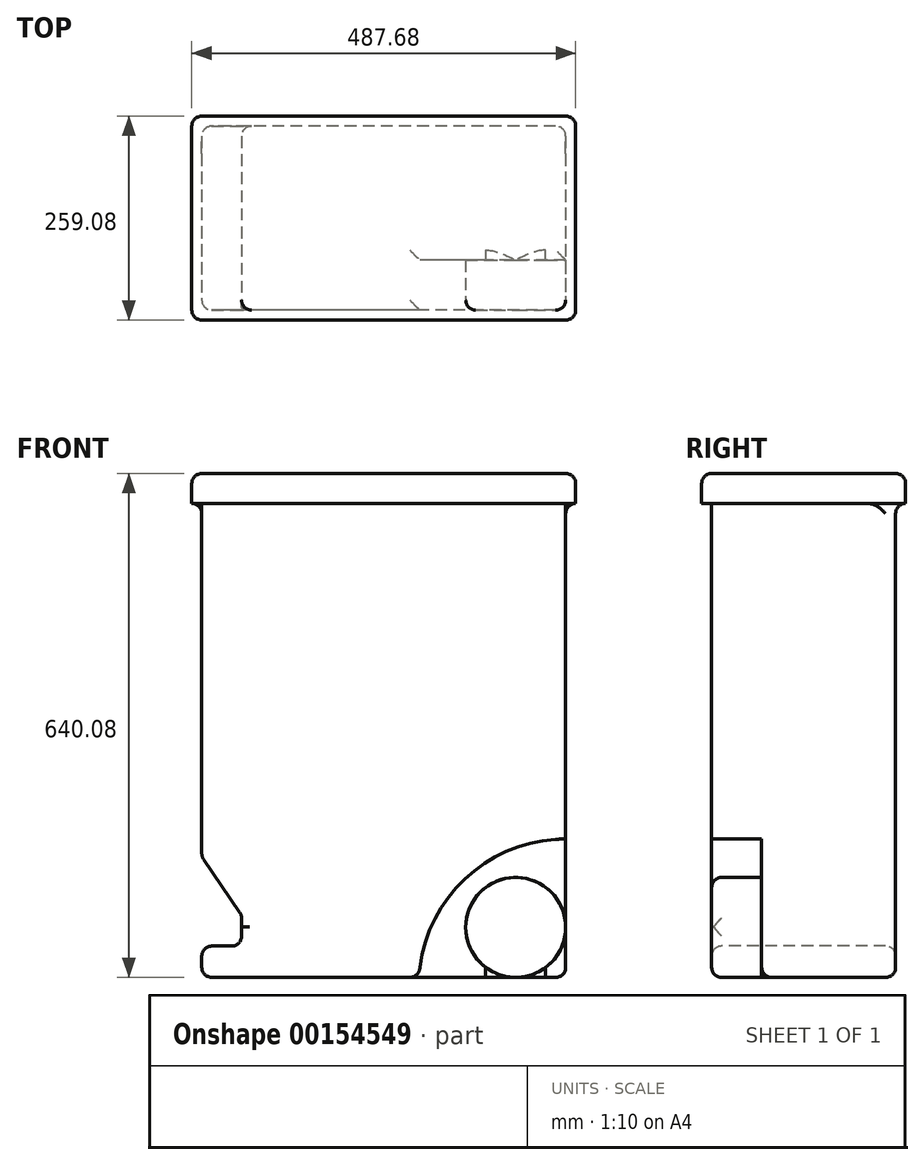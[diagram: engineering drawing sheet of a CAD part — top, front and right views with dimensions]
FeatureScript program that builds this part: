
annotation { "Feature Type Name" : "Feature", "Feature Type Description" : "" }
export const myFeature = defineFeature(function(context is Context, id is Id, definition is map)
    precondition{}
    {
        {
            var Q0;
            Q0=qCreatedBy(makeId("Top.planeOp"),FACE);
            var sketch = newSketch(context, id + "F0", { "sketchPlane" : qUnion([Q0])});
            skLineSegment(sketch, "E0.bottom", {"start": v(231.14, 116.84) * mm, "end": v(-231.14, 116.84) * mm});
            skLineSegment(sketch, "E0.top", {"start": v(231.14, -116.84) * mm, "end": v(-231.14, -116.84) * mm});
            skLineSegment(sketch, "E0.left", {"start": v(231.14, 116.84) * mm, "end": v(231.14, -116.84) * mm});
            skLineSegment(sketch, "E0.right", {"start": v(-231.14, 116.84) * mm, "end": v(-231.14, -116.84) * mm});
            skPoint(sketch, "E0.middle", {"position": v(0, 0) * mm});
            skSolve(sketch);
        }
        {
            var Q0;
            Q0=makeQuery(id+"F0.imprint","IMPRINT",FACE,{"disambiguationData":[TD([[makeQuery(id+"F0.imprint","IMPRINT",EDGE,{"derivedFrom":sQuery(id+"F0.wireOp",EDGE,"E0.bottom")}),1.0]])]});
            extrude(context, id + "F1", {"entities" : qUnion([Q0]), "depth" : 640.08 * mm});
        }
        {
            var Q0;
            Q0=makeQuery(id+"F1.opExtrude","CAP_FACE",FACE,{"disambiguationData":[OSD([sQuery(id+"F0.wireOp",EDGE,"E0.bottom"),sQuery(id+"F0.wireOp",EDGE,"E0.top"),sQuery(id+"F0.wireOp",EDGE,"E0.left"),sQuery(id+"F0.wireOp",EDGE,"E0.right")])],"isStart":false});
            var sketch = newSketch(context, id + "F2", { "sketchPlane" : qUnion([Q0])});
            skLineSegment(sketch, "E1.0", {"start": v(243.84, -129.54) * mm, "end": v(-243.84, -129.54) * mm});
            skLineSegment(sketch, "E1.1", {"start": v(243.84, 129.54) * mm, "end": v(243.84, -129.54) * mm});
            skLineSegment(sketch, "E1.2", {"start": v(243.84, 129.54) * mm, "end": v(-243.84, 129.54) * mm});
            skLineSegment(sketch, "E1.3", {"start": v(-243.84, 129.54) * mm, "end": v(-243.84, -129.54) * mm});
            skSolve(sketch);
        }
        {
            var Q0;
            Q0=makeQuery(id+"F2.imprint","IMPRINT",FACE,{"disambiguationData":[TD([[makeQuery(id+"F2.imprint","IMPRINT",EDGE,{"derivedFrom":sQuery(id+"F2.wireOp",EDGE,"E1.0")}),-1.0]])]});
            extrude(context, id + "F3", {"entities" : qUnion([Q0]), "operationType" : NewBodyOperationType.ADD, "oppositeDirection" : true, "depth" : 38.1 * mm});
        }
        {
            var Q0;
            Q0=qCreatedBy(makeId("Front.planeOp"),FACE);
            var sketch = newSketch(context, id + "F4", { "sketchPlane" : qUnion([Q0])});
            skLineSegment(sketch, "E2", {"start": v(-231.14, 153.28) * mm, "end": v(-180.63, 79.53) * mm});
            skLineSegment(sketch, "E3", {"start": v(-180.63, 79.53) * mm, "end": v(-180.63, 0) * mm});
            skLineSegment(sketch, "E4.0", {"start": v(231.14, 0) * mm, "end": v(-231.14, 0) * mm});
            skLineSegment(sketch, "E4.1", {"start": v(-231.14, 601.98) * mm, "end": v(-231.14, 0) * mm});
            skLineSegment(sketch, "E5", {"start": v(-180.63, 39.77) * mm, "end": v(-231.14, 39.77) * mm});
            skSolve(sketch);
        }
        {
            var Q0;
            {var subQ0=sQuery(id+"F4.wireOp",EDGE,"E2");Q0=makeQuery(id+"F4.imprint","IMPRINT",FACE,{"disambiguationData":[TD([[makeQuery(id+"F4.imprint","IMPRINT",EDGE,{"derivedFrom":subQ0}),-1.0]])]});}
            extrude(context, id + "F5", {"entities" : qUnion([Q0]), "operationType" : NewBodyOperationType.REMOVE, "oppositeDirection" : true, "depth" : 304.8 * mm, "symmetric" : true});
        }
        {
            var Q0;
            Q0=makeQuery(id+"F1.opExtrude","SWEPT_FACE",FACE,{"disambiguationData":[OSD([sQuery(id+"F0.wireOp",EDGE,"E0.top")])]});
            var sketch = newSketch(context, id + "F6", { "sketchPlane" : qUnion([Q0])});
            skCircle(sketch, "E6", {"center": v(167.64, 63.5) * mm, "radius": 63.5 * mm});
            skCircle(sketch, "E7", {"center": v(231.14, -10.9) * mm, "radius": 186.7 * mm});
            skLineSegment(sketch, "E8.0", {"start": v(231.14, 601.98) * mm, "end": v(231.14, 0) * mm});
            skLineSegment(sketch, "E8.1", {"start": v(231.14, 0) * mm, "end": v(-231.14, 0) * mm});
            skSolve(sketch);
        }
        {
            var Q0;
            {var subQ0=sQuery(id+"F6.wireOp",EDGE,"E8.0");var subQ1=sQuery(id+"F6.wireOp",EDGE,"E6");var subQ2=makeQuery(id+"F6.imprint","INTERSECT",VERTEX,{"derivedFrom":[subQ1,subQ0]});Q0=makeQuery(id+"F6.imprint","IMPRINT",FACE,{"disambiguationData":[TD([[makeQuery(id+"F6.imprint","IMPRINT",EDGE,{"disambiguationData":[TD([[subQ2,-1.0]])],"derivedFrom":subQ1}),-1.0]])]});}
            var Q1;
            {var subQ0=sQuery(id+"F6.wireOp",EDGE,"E8.0");var subQ1=sQuery(id+"F6.wireOp",EDGE,"E6");var subQ2=makeQuery(id+"F6.imprint","INTERSECT",VERTEX,{"derivedFrom":[subQ1,subQ0]});Q1=makeQuery(id+"F6.imprint","IMPRINT",FACE,{"disambiguationData":[TD([[makeQuery(id+"F6.imprint","IMPRINT",EDGE,{"disambiguationData":[TD([[subQ2,1.0]])],"derivedFrom":subQ1}),-1.0]])]});}
            extrude(context, id + "F7", {"entities" : qUnion([Q0, Q1]), "operationType" : NewBodyOperationType.REMOVE, "oppositeDirection" : true, "depth" : 63.5 * mm});
        }
        {
            var Q0;
            Q0=makeQuery(id+"F1.opExtrude","SWEPT_EDGE",EDGE,{"disambiguationData":[OSD([sQuery(id+"F0.wireOp",EDGE,"E0.top"),sQuery(id+"F0.wireOp",EDGE,"E0.right")])]});
            var Q1;
            Q1=makeQuery(id+"F1.opExtrude","SWEPT_EDGE",EDGE,{"disambiguationData":[OSD([sQuery(id+"F0.wireOp",EDGE,"E0.bottom"),sQuery(id+"F0.wireOp",EDGE,"E0.right")])]});
            var Q2;
            Q2=makeQuery(id+"F1.opExtrude","SWEPT_EDGE",EDGE,{"disambiguationData":[OSD([sQuery(id+"F0.wireOp",EDGE,"E0.bottom"),sQuery(id+"F0.wireOp",EDGE,"E0.left")])]});
            var Q3;
            Q3=makeQuery(id+"F1.opExtrude","SWEPT_EDGE",EDGE,{"disambiguationData":[OSD([sQuery(id+"F0.wireOp",EDGE,"E0.top"),sQuery(id+"F0.wireOp",EDGE,"E0.left")])]});
            var Q4;
            {var subQ0=sQuery(id+"F0.wireOp",EDGE,"E0.right");var subQ1=sQuery(id+"F0.wireOp",EDGE,"E0.left");var subQ2=sQuery(id+"F0.wireOp",EDGE,"E0.top");var subQ3=sQuery(id+"F0.wireOp",EDGE,"E0.bottom");Q4=makeQuery(id+"F3.boolean.opBoolean","MERGE",FACE,{"derivedFrom":[makeQuery(id+"F1.opExtrude","CAP_FACE",FACE,{"disambiguationData":[OSD([subQ3,subQ2,subQ1,subQ0])],"isStart":false}),makeQuery(id+"F3.opExtrude","CAP_FACE",FACE,{"disambiguationData":[OSD([subQ3,subQ2,subQ1,subQ0,sQuery(id+"F2.wireOp",EDGE,"E1.0"),sQuery(id+"F2.wireOp",EDGE,"E1.1"),sQuery(id+"F2.wireOp",EDGE,"E1.2"),sQuery(id+"F2.wireOp",EDGE,"E1.3")])],"isStart":true})]});}
            var Q5;
            Q5=makeQuery(id+"F3.opExtrude","SWEPT_EDGE",EDGE,{"disambiguationData":[OSD([sQuery(id+"F2.wireOp",EDGE,"E1.1"),sQuery(id+"F2.wireOp",EDGE,"E1.2")])]});
            var Q6;
            Q6=makeQuery(id+"F3.opExtrude","SWEPT_EDGE",EDGE,{"disambiguationData":[OSD([sQuery(id+"F2.wireOp",EDGE,"E1.2"),sQuery(id+"F2.wireOp",EDGE,"E1.3")])]});
            var Q7;
            Q7=makeQuery(id+"F3.opExtrude","SWEPT_EDGE",EDGE,{"disambiguationData":[OSD([sQuery(id+"F2.wireOp",EDGE,"E1.0"),sQuery(id+"F2.wireOp",EDGE,"E1.1")])]});
            var Q8;
            Q8=makeQuery(id+"F3.opExtrude","SWEPT_EDGE",EDGE,{"disambiguationData":[OSD([sQuery(id+"F2.wireOp",EDGE,"E1.0"),sQuery(id+"F2.wireOp",EDGE,"E1.3")])]});
            var Q9;
            Q9=makeQuery(id+"F5.boolean.opBoolean","COPY",EDGE,{"derivedFrom":makeQuery(id+"F5.opExtrude","SWEPT_EDGE",EDGE,{"disambiguationData":[OSD([sQuery(id+"F4.wireOp",EDGE,"E2"),sQuery(id+"F4.wireOp",EDGE,"E4.1")])]})});
            var Q10;
            Q10=makeQuery(id+"F5.boolean.opBoolean","COPY",FACE,{"derivedFrom":makeQuery(id+"F5.opExtrude","SWEPT_FACE",FACE,{"disambiguationData":[OSD([sQuery(id+"F4.wireOp",EDGE,"E2")])]})});
            var Q11;
            Q11=makeQuery(id+"F5.boolean.opBoolean","COPY",EDGE,{"derivedFrom":makeQuery(id+"F5.opExtrude","SWEPT_EDGE",EDGE,{"disambiguationData":[OSD([sQuery(id+"F4.wireOp",EDGE,"E4.1"),sQuery(id+"F4.wireOp",EDGE,"E5")])]})});
            var Q12;
            Q12=makeQuery(id+"F5.boolean.opBoolean","COPY",FACE,{"derivedFrom":makeQuery(id+"F5.opExtrude","SWEPT_FACE",FACE,{"disambiguationData":[OSD([sQuery(id+"F4.wireOp",EDGE,"E5")])]})});
            var Q13;
            Q13=makeQuery(id+"FMVX19U1BdIDMrO_1.1.F7.boolean.opBoolean","COPY",EDGE,{"derivedFrom":makeQuery(id+"FMVX19U1BdIDMrO_1.1.F7.opExtrude","CAP_EDGE",EDGE,{"disambiguationData":[OSD([sQuery(id+"F6.wireOp",EDGE,"E7")])],"isStart":true})});
            var Q14;
            {var subQ0=sQuery(id+"F6.wireOp",EDGE,"E6");var subQ1=makeQuery(id+"F6.imprint","INTERSECT",VERTEX,{"derivedFrom":[subQ0,sQuery(id+"F6.wireOp",EDGE,"E8.0")]});Q14=makeQuery(id+"FMVX19U1BdIDMrO_1.1.F7.boolean.opBoolean","SPLIT",FACE,{"disambiguationData":[TD([makeQuery(id+"FMVX19U1BdIDMrO_1.1.F7.opExtrude","SWEPT_FACE",FACE,{"disambiguationData":[OSD([subQ0]),TDD([makeQuery(id+"F6.imprint","IMPRINT",EDGE,{"disambiguationData":[TD([[subQ1,-1.0]])],"derivedFrom":subQ0})])]})])],"derivedFrom":makeQuery(id+"F1.opExtrude","SWEPT_FACE",FACE,{"disambiguationData":[OSD([sQuery(id+"F0.wireOp",EDGE,"E0.bottom")])]})});}
            var Q15;
            Q15=makeQuery(id+"FMVX19U1BdIDMrO_1.1.F7.boolean.opBoolean","COPY",EDGE,{"derivedFrom":makeQuery(id+"FMVX19U1BdIDMrO_1.1.F7.opExtrude","SWEPT_EDGE",EDGE,{"disambiguationData":[OSD([sQuery(id+"F6.wireOp",EDGE,"E7"),sQuery(id+"F6.wireOp",EDGE,"E8.1")])]})});
            var Q16;
            Q16=makeQuery(id+"FMVX19U1BdIDMrO_1.1.F7.boolean.opBoolean","COPY",EDGE,{"derivedFrom":makeQuery(id+"FMVX19U1BdIDMrO_1.1.F7.opExtrude","SWEPT_EDGE",EDGE,{"disambiguationData":[OSD([sQuery(id+"F6.wireOp",EDGE,"E7"),sQuery(id+"F6.wireOp",EDGE,"E8.0")])]})});
            var Q17;
            {var subQ0=sQuery(id+"F6.wireOp",EDGE,"E6");var subQ1=makeQuery(id+"F6.imprint","INTERSECT",VERTEX,{"derivedFrom":[subQ0,sQuery(id+"F6.wireOp",EDGE,"E8.0")]});Q17=makeQuery(id+"F7.boolean.opBoolean","SPLIT",FACE,{"disambiguationData":[TD([makeQuery(id+"F7.opExtrude","SWEPT_FACE",FACE,{"disambiguationData":[OSD([subQ0]),TDD([makeQuery(id+"F6.imprint","IMPRINT",EDGE,{"disambiguationData":[TD([[subQ1,-1.0]])],"derivedFrom":subQ0})])]})])],"derivedFrom":makeQuery(id+"F1.opExtrude","SWEPT_FACE",FACE,{"disambiguationData":[OSD([sQuery(id+"F0.wireOp",EDGE,"E0.top")])]})});}
            var Q18;
            Q18=makeQuery(id+"F7.boolean.opBoolean","COPY",EDGE,{"derivedFrom":makeQuery(id+"F7.opExtrude","CAP_EDGE",EDGE,{"disambiguationData":[OSD([sQuery(id+"F6.wireOp",EDGE,"E7")])],"isStart":true})});
            var Q19;
            Q19=makeQuery(id+"F7.boolean.opBoolean","COPY",EDGE,{"derivedFrom":makeQuery(id+"F7.opExtrude","SWEPT_EDGE",EDGE,{"disambiguationData":[OSD([sQuery(id+"F6.wireOp",EDGE,"E7"),sQuery(id+"F6.wireOp",EDGE,"E8.0")])]})});
            var Q20;
            Q20=makeQuery(id+"F7.boolean.opBoolean","COPY",EDGE,{"derivedFrom":makeQuery(id+"F7.opExtrude","SWEPT_EDGE",EDGE,{"disambiguationData":[OSD([sQuery(id+"F6.wireOp",EDGE,"E7"),sQuery(id+"F6.wireOp",EDGE,"E8.1")])]})});
            var Q21;
            {var subQ0=sQuery(id+"F6.wireOp",EDGE,"E8.0");Q21=makeQuery(id+"F7.boolean.opBoolean","COPY",EDGE,{"derivedFrom":makeQuery(id+"F7.opExtrude","CAP_EDGE",EDGE,{"disambiguationData":[OSD([subQ0]),TDD([makeQuery(id+"F6.imprint","IMPRINT",EDGE,{"disambiguationData":[TD([[makeQuery(id+"F6.imprint","INTERSECT",VERTEX,{"derivedFrom":[sQuery(id+"F6.wireOp",EDGE,"E7"),subQ0]}),-1.0]])],"derivedFrom":subQ0})])],"isStart":false})});}
            var Q22;
            {var subQ0=sQuery(id+"F6.wireOp",EDGE,"E8.0");Q22=makeQuery(id+"FMVX19U1BdIDMrO_1.1.F7.boolean.opBoolean","COPY",EDGE,{"derivedFrom":makeQuery(id+"FMVX19U1BdIDMrO_1.1.F7.opExtrude","CAP_EDGE",EDGE,{"disambiguationData":[OSD([subQ0]),TDD([makeQuery(id+"F6.imprint","IMPRINT",EDGE,{"disambiguationData":[TD([[makeQuery(id+"F6.imprint","INTERSECT",VERTEX,{"derivedFrom":[sQuery(id+"F6.wireOp",EDGE,"E7"),subQ0]}),-1.0]])],"derivedFrom":subQ0})])],"isStart":false})});}
            var Q23;
            Q23=makeQuery(id+"F1.opExtrude","CAP_FACE",FACE,{"disambiguationData":[OSD([sQuery(id+"F0.wireOp",EDGE,"E0.bottom"),sQuery(id+"F0.wireOp",EDGE,"E0.top"),sQuery(id+"F0.wireOp",EDGE,"E0.left"),sQuery(id+"F0.wireOp",EDGE,"E0.right")])],"isStart":true});
            fillet(context, id + "F8", {"entities" : qUnion([Q0, Q1, Q2, Q3, Q4, Q5, Q6, Q7, Q8, Q9, Q10, Q11, Q12, Q13, Q14, Q15, Q16, Q17, Q18, Q19, Q20, Q21, Q22, Q23]), "radius" : 12.7 * mm, "tangentPropagation" : true, "allowEdgeOverflow" : false});
        }
    });
